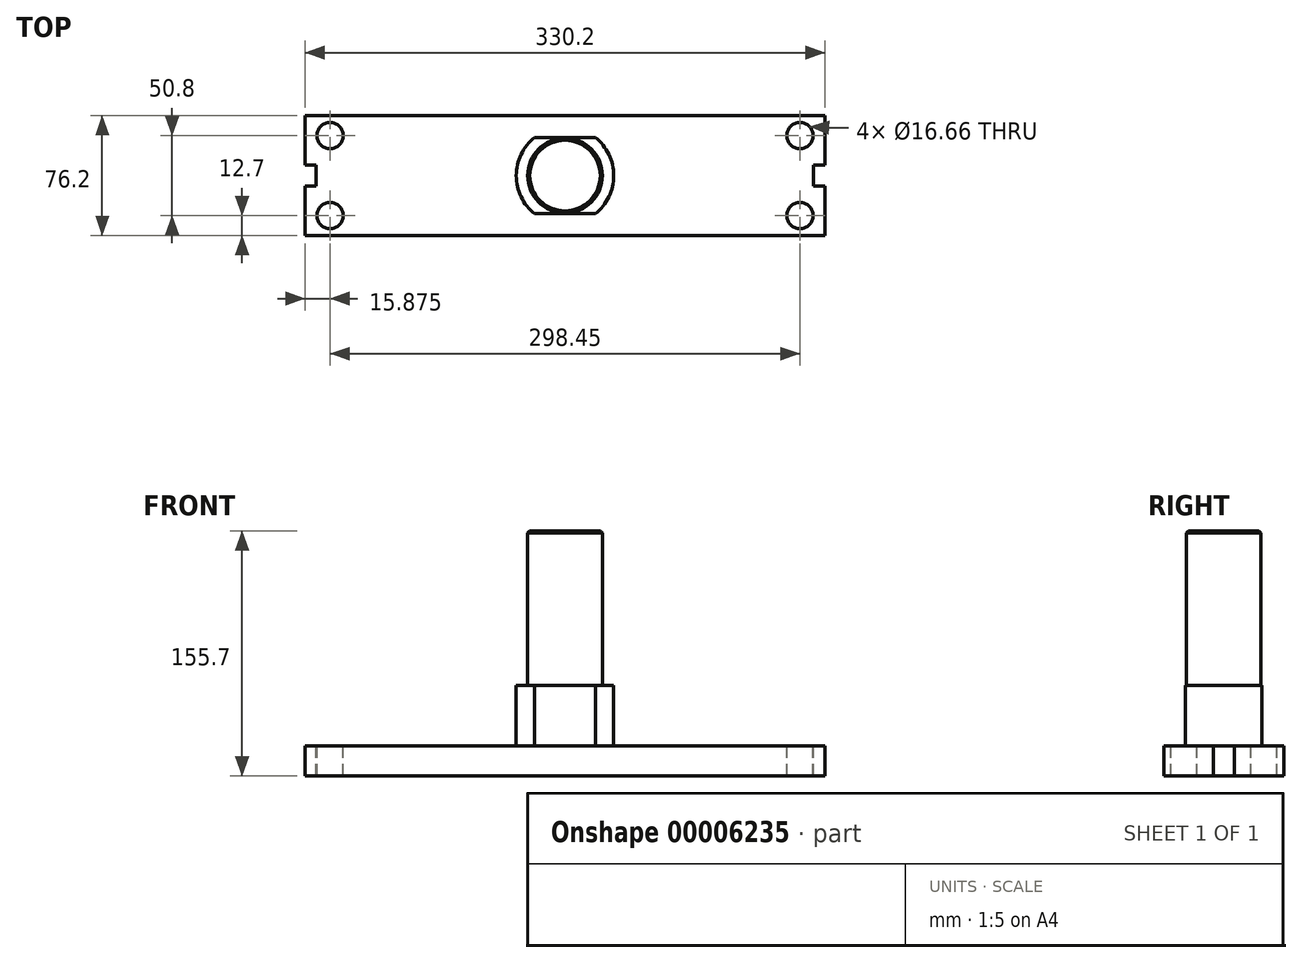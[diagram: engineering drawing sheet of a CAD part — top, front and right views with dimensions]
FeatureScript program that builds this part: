
annotation { "Feature Type Name" : "Feature", "Feature Type Description" : "" }
export const myFeature = defineFeature(function(context is Context, id is Id, definition is map)
    precondition{}
    {
        {
            var Q0;
            Q0=qCreatedBy(makeId("Top.planeOp"),FACE);
            var sketch = newSketch(context, id + "F0", { "sketchPlane" : qUnion([Q0])});
            skLineSegment(sketch, "E0.bottom", {"start": v(0, 0) * mm, "end": v(-330.2, 0) * mm});
            skLineSegment(sketch, "E0.top", {"start": v(0, -76.2) * mm, "end": v(-330.2, -76.2) * mm});
            skLineSegment(sketch, "E0.left", {"start": v(0, 0) * mm, "end": v(0, -31.34) * mm});
            skLineSegment(sketch, "E0.right", {"start": v(-330.2, 0) * mm, "end": v(-330.2, -31.34) * mm});
            skLineSegment(sketch, "E1.0", {"start": v(-323.06, -31.34) * mm, "end": v(-323.06, -44.84) * mm});
            skLineSegment(sketch, "E2.0", {"start": v(-7.14, -31.34) * mm, "end": v(-7.14, -44.84) * mm});
            skLineSegment(sketch, "E3.0", {"start": v(-330.2, -44.84) * mm, "end": v(-323.06, -44.84) * mm});
            skLineSegment(sketch, "E4.0", {"start": v(-330.2, -31.34) * mm, "end": v(-323.06, -31.34) * mm});
            skPoint(sketch, "E5.orphan", {"position": v(-330.2, -38.1) * mm});
            skLineSegment(sketch, "E6.trimOffspring", {"start": v(-330.2, -44.84) * mm, "end": v(-330.2, -76.2) * mm});
            skLineSegment(sketch, "E7.trimOffspring", {"start": v(-7.14, -44.84) * mm, "end": v(0, -44.84) * mm});
            skLineSegment(sketch, "E8.trimOffspring", {"start": v(-7.14, -31.34) * mm, "end": v(0, -31.34) * mm});
            skLineSegment(sketch, "E9.trimOffspring", {"start": v(0, -44.84) * mm, "end": v(0, -76.2) * mm});
            skLineSegment(sketch, "E10", {"start": v(-165.1, 0) * mm, "end": v(-165.1, -76.2) * mm, "construction": true});
            skCircle(sketch, "E11", {"center": v(-15.87, -12.7) * mm, "radius": 8.33 * mm});
            skCircle(sketch, "E12", {"center": v(-15.87, -63.5) * mm, "radius": 8.33 * mm});
            skCircle(sketch, "E13.0.MirrorC", {"center": v(-314.33, -12.7) * mm, "radius": 8.33 * mm});
            skCircle(sketch, "E14.0.MirrorC", {"center": v(-314.33, -63.5) * mm, "radius": 8.33 * mm});
            skCircle(sketch, "E15", {"center": v(-165.1, -38.1) * mm, "radius": 17.46 * mm});
            skSolve(sketch);
        }
        {
            var Q0;
            Q0=makeQuery(id+"F0.imprint","IMPRINT",FACE,{"disambiguationData":[TD([[makeQuery(id+"F0.imprint","IMPRINT",EDGE,{"derivedFrom":sQuery(id+"F0.wireOp",EDGE,"E0.bottom")}),1.0]])]});
            extrude(context, id + "F1", {"entities" : qUnion([Q0]), "oppositeDirection" : true, "depth" : 19.05 * mm});
        }
        {
            var Q0;
            Q0=qCreatedBy(makeId("Top.planeOp"),FACE);
            var sketch = newSketch(context, id + "F2", { "sketchPlane" : qUnion([Q0])});
            skCircle(sketch, "E16.0", {"center": v(-165.1, -38.1) * mm, "radius": 17.46 * mm});
            skSolve(sketch);
        }
        {
            var Q0;
            Q0 = qSketchRegion(id + "F2", true);
            extrude(context, id + "F3", {"entities" : qUnion([Q0]), "oppositeDirection" : true, "depth" : 19.05 * mm});
        }
        {
            var Q0;
            Q0=makeQuery(id+"F3.opExtrude","CAP_FACE",FACE,{"disambiguationData":[OSD([sQuery(id+"F2.wireOp",EDGE,"E16.0")])],"isStart":true});
            var sketch = newSketch(context, id + "F4", { "sketchPlane" : qUnion([Q0])});
            skArc(sketch, "E17", {"start": v(-145.88, -62.36) * mm, "mid": v(-134.15, -38.1) * mm, "end": v(-145.88, -13.84) * mm});
            skLineSegment(sketch, "E18", {"start": v(-184.32, -13.84) * mm, "end": v(-145.88, -13.84) * mm});
            skLineSegment(sketch, "E19.0", {"start": v(-184.32, -62.36) * mm, "end": v(-145.88, -62.36) * mm});
            skPoint(sketch, "E20.orphan", {"position": v(-129.82, -13.84) * mm});
            skArc(sketch, "E21.trimOffspring", {"start": v(-184.32, -13.84) * mm, "mid": v(-196.05, -38.1) * mm, "end": v(-184.32, -62.36) * mm});
            skSolve(sketch);
        }
        {
            var Q0;
            Q0 = qSketchRegion(id + "F4", true);
            extrude(context, id + "F5", {"entities" : qUnion([Q0]), "operationType" : NewBodyOperationType.ADD, "depth" : 38.48 * mm});
        }
        {
            var Q0;
            Q0=makeQuery(id+"F5.opExtrude","CAP_FACE",FACE,{"disambiguationData":[OSD([sQuery(id+"F4.wireOp",EDGE,"E17"),sQuery(id+"F4.wireOp",EDGE,"E18"),sQuery(id+"F4.wireOp",EDGE,"E19.0"),sQuery(id+"F4.wireOp",EDGE,"E21.trimOffspring")])],"isStart":false});
            var sketch = newSketch(context, id + "F6", { "sketchPlane" : qUnion([Q0])});
            skCircle(sketch, "E22", {"center": v(-165.1, -38.1) * mm, "radius": 23.69 * mm});
            skSolve(sketch);
        }
        {
            var Q0;
            Q0 = qSketchRegion(id + "F6", true);
            extrude(context, id + "F7", {"entities" : qUnion([Q0]), "operationType" : NewBodyOperationType.ADD, "depth" : 98.17 * mm});
        }
        {
            var Q0;
            Q0=makeQuery(id+"F7.opExtrude","CAP_EDGE",EDGE,{"disambiguationData":[OSD([sQuery(id+"F6.wireOp",EDGE,"E22")])],"isStart":false});
            chamfer(context, id + "F8", {"entities" : qUnion([Q0]), "width" : 1.27 * mm, "tangentPropagation" : true});
        }
    });
